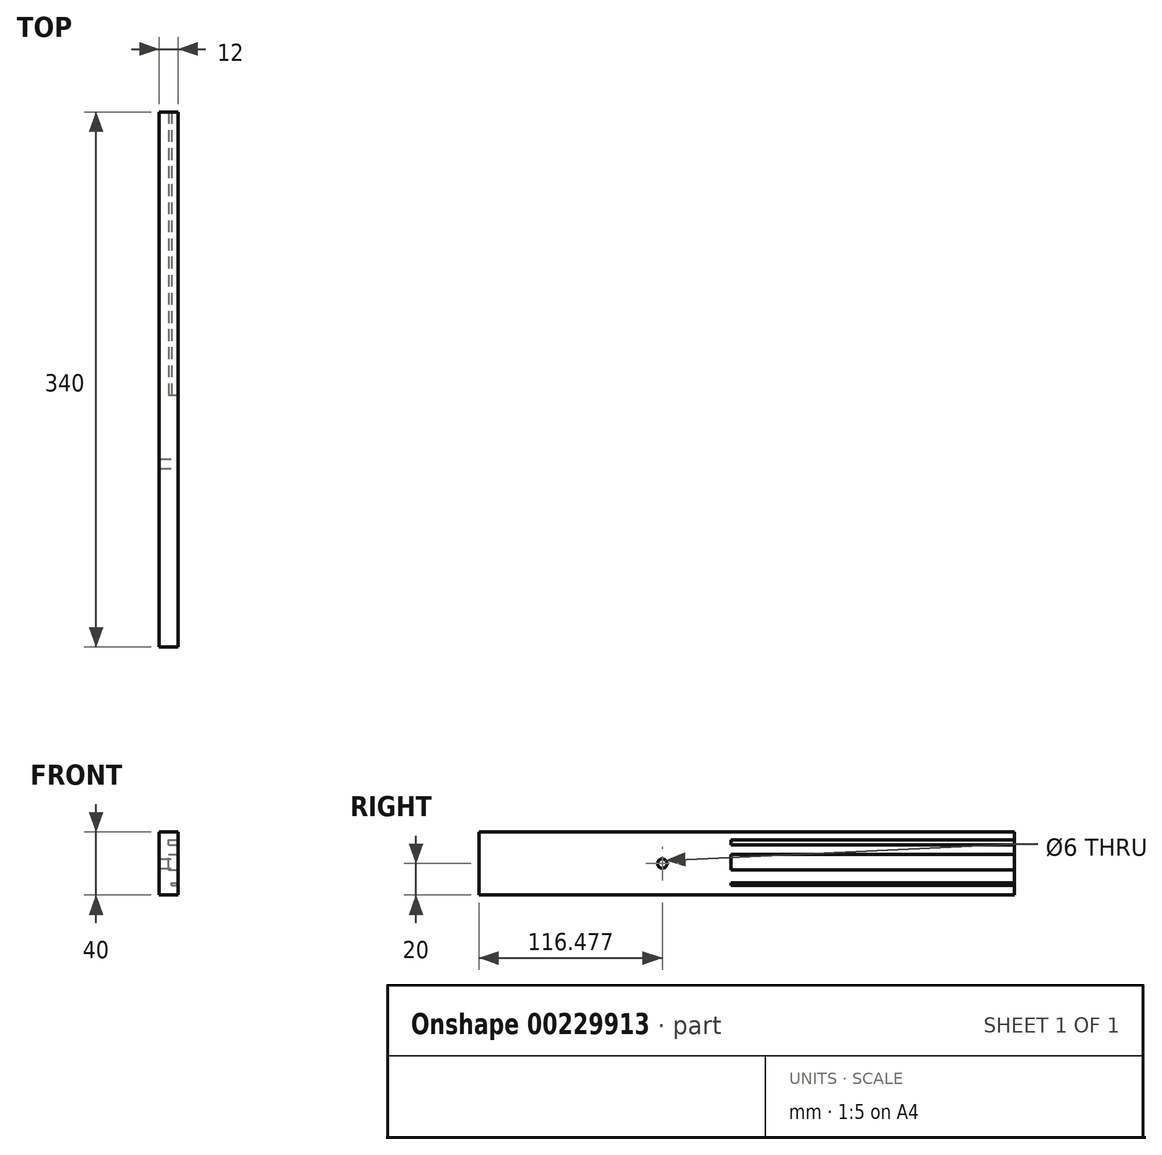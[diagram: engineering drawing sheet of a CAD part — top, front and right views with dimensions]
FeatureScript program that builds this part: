
annotation { "Feature Type Name" : "Feature", "Feature Type Description" : "" }
export const myFeature = defineFeature(function(context is Context, id is Id, definition is map)
    precondition{}
    {
        {
            var Q0;
            Q0=qCreatedBy(makeId("Right.planeOp"),FACE);
            var sketch = newSketch(context, id + "F0", { "sketchPlane" : qUnion([Q0])});
            skLineSegment(sketch, "E0.bottom", {"start": v(0, 0) * mm, "end": v(340, 0) * mm});
            skLineSegment(sketch, "E0.top", {"start": v(0, 40) * mm, "end": v(340, 40) * mm});
            skLineSegment(sketch, "E0.left", {"start": v(0, 0) * mm, "end": v(0, 40) * mm});
            skLineSegment(sketch, "E0.right", {"start": v(340, 0) * mm, "end": v(340, 40) * mm});
            skSolve(sketch);
        }
        {
            var Q0;
            Q0=qSketchRegion(id+"F0",true);
            extrude(context, id + "F1", {"entities" : qUnion([Q0]), "endBound" : BoundingType.SYMMETRIC, "depth" : 12 * mm});
        }
        {
            var Q0;
            Q0=makeQuery(id+"F1.opExtrude","CAP_FACE",FACE,{"disambiguationData":[OSD([sQuery(id+"F0.wireOp",EDGE,"E0.bottom"),sQuery(id+"F0.wireOp",EDGE,"E0.top"),sQuery(id+"F0.wireOp",EDGE,"E0.left"),sQuery(id+"F0.wireOp",EDGE,"E0.right")])],"isStart":false});
            var sketch = newSketch(context, id + "F2", { "sketchPlane" : qUnion([Q0])});
            skLineSegment(sketch, "E1.bottom", {"start": v(340, 35) * mm, "end": v(160, 35) * mm});
            skLineSegment(sketch, "E1.top", {"start": v(340, 32) * mm, "end": v(160, 32) * mm});
            skLineSegment(sketch, "E1.left", {"start": v(340, 35) * mm, "end": v(340, 32) * mm});
            skLineSegment(sketch, "E1.right", {"start": v(160, 35) * mm, "end": v(160, 32) * mm});
            skSolve(sketch);
        }
        {
            var Q0;
            Q0=qSketchRegion(id+"F2",true);
            extrude(context, id + "F3", {"entities" : qUnion([Q0]), "operationType" : NewBodyOperationType.REMOVE, "oppositeDirection" : true, "depth" : 6 * mm});
        }
        {
            var Q0;
            Q0=makeQuery(id+"F1.opExtrude","CAP_FACE",FACE,{"disambiguationData":[OSD([sQuery(id+"F0.wireOp",EDGE,"E0.bottom"),sQuery(id+"F0.wireOp",EDGE,"E0.top"),sQuery(id+"F0.wireOp",EDGE,"E0.left"),sQuery(id+"F0.wireOp",EDGE,"E0.right")])],"isStart":false});
            var sketch = newSketch(context, id + "F4", { "sketchPlane" : qUnion([Q0])});
            skCircle(sketch, "E2", {"center": v(116.48, 20) * mm, "radius": 3 * mm});
            skPoint(sketch, "E2.centerSnap0", {"position": v(0, 20) * mm});
            skSolve(sketch);
        }
        {
            var Q0;
            Q0=sQuery(id+"F4.wireOp",VERTEX,"E2.center");
            var Q1;
            Q1=makeQuery(id+"F1.opExtrude","SWEPT_BODY",BODY,{"disambiguationData":[OSD([sQuery(id+"F0.wireOp",EDGE,"E0.bottom"),sQuery(id+"F0.wireOp",EDGE,"E0.top"),sQuery(id+"F0.wireOp",EDGE,"E0.left"),sQuery(id+"F0.wireOp",EDGE,"E0.right")])]});
            hole(context, id + "F5", {"style" : HoleStyle.SIMPLE, "endStyle" : HoleEndStyle.THROUGH, "holeDiameter" : 6 * mm, "locations" : qUnion([Q0]), "scope" : qUnion([Q1]), "isTappedThrough" : true});
        }
        {
            var Q0;
            Q0=makeQuery(id+"F1.opExtrude","CAP_FACE",FACE,{"disambiguationData":[OSD([sQuery(id+"F0.wireOp",EDGE,"E0.bottom"),sQuery(id+"F0.wireOp",EDGE,"E0.top"),sQuery(id+"F0.wireOp",EDGE,"E0.left"),sQuery(id+"F0.wireOp",EDGE,"E0.right")])],"isStart":false});
            var sketch = newSketch(context, id + "F6", { "sketchPlane" : qUnion([Q0])});
            skPoint(sketch, "E3.oppositeSnap0", {"position": v(340, 16) * mm});
            skLineSegment(sketch, "E3.bottom", {"start": v(340, 26) * mm, "end": v(160, 26) * mm});
            skLineSegment(sketch, "E3.top", {"start": v(340, 16) * mm, "end": v(160, 16) * mm});
            skLineSegment(sketch, "E3.left", {"start": v(340, 26) * mm, "end": v(340, 16) * mm});
            skLineSegment(sketch, "E3.right", {"start": v(160, 26) * mm, "end": v(160, 16) * mm});
            skSolve(sketch);
        }
        {
            var Q0;
            Q0=qSketchRegion(id+"F6",true);
            extrude(context, id + "F7", {"entities" : qUnion([Q0]), "operationType" : NewBodyOperationType.REMOVE, "oppositeDirection" : true, "depth" : 6 * mm});
        }
        {
            var Q0;
            Q0=makeQuery(id+"F1.opExtrude","CAP_FACE",FACE,{"disambiguationData":[OSD([sQuery(id+"F0.wireOp",EDGE,"E0.bottom"),sQuery(id+"F0.wireOp",EDGE,"E0.top"),sQuery(id+"F0.wireOp",EDGE,"E0.left"),sQuery(id+"F0.wireOp",EDGE,"E0.right")])],"isStart":false});
            var sketch = newSketch(context, id + "F8", { "sketchPlane" : qUnion([Q0])});
            skLineSegment(sketch, "E4.bottom", {"start": v(340, 6.06) * mm, "end": v(160, 6.06) * mm});
            skLineSegment(sketch, "E4.top", {"start": v(340, 7.66) * mm, "end": v(160, 7.66) * mm});
            skLineSegment(sketch, "E4.left", {"start": v(340, 6.06) * mm, "end": v(340, 7.66) * mm});
            skLineSegment(sketch, "E4.right", {"start": v(160, 6.06) * mm, "end": v(160, 7.66) * mm});
            skSolve(sketch);
        }
        {
            var Q0;
            Q0=qSketchRegion(id+"F8",true);
            extrude(context, id + "F9", {"entities" : qUnion([Q0]), "operationType" : NewBodyOperationType.REMOVE, "oppositeDirection" : true, "depth" : 4 * mm});
        }
    });
